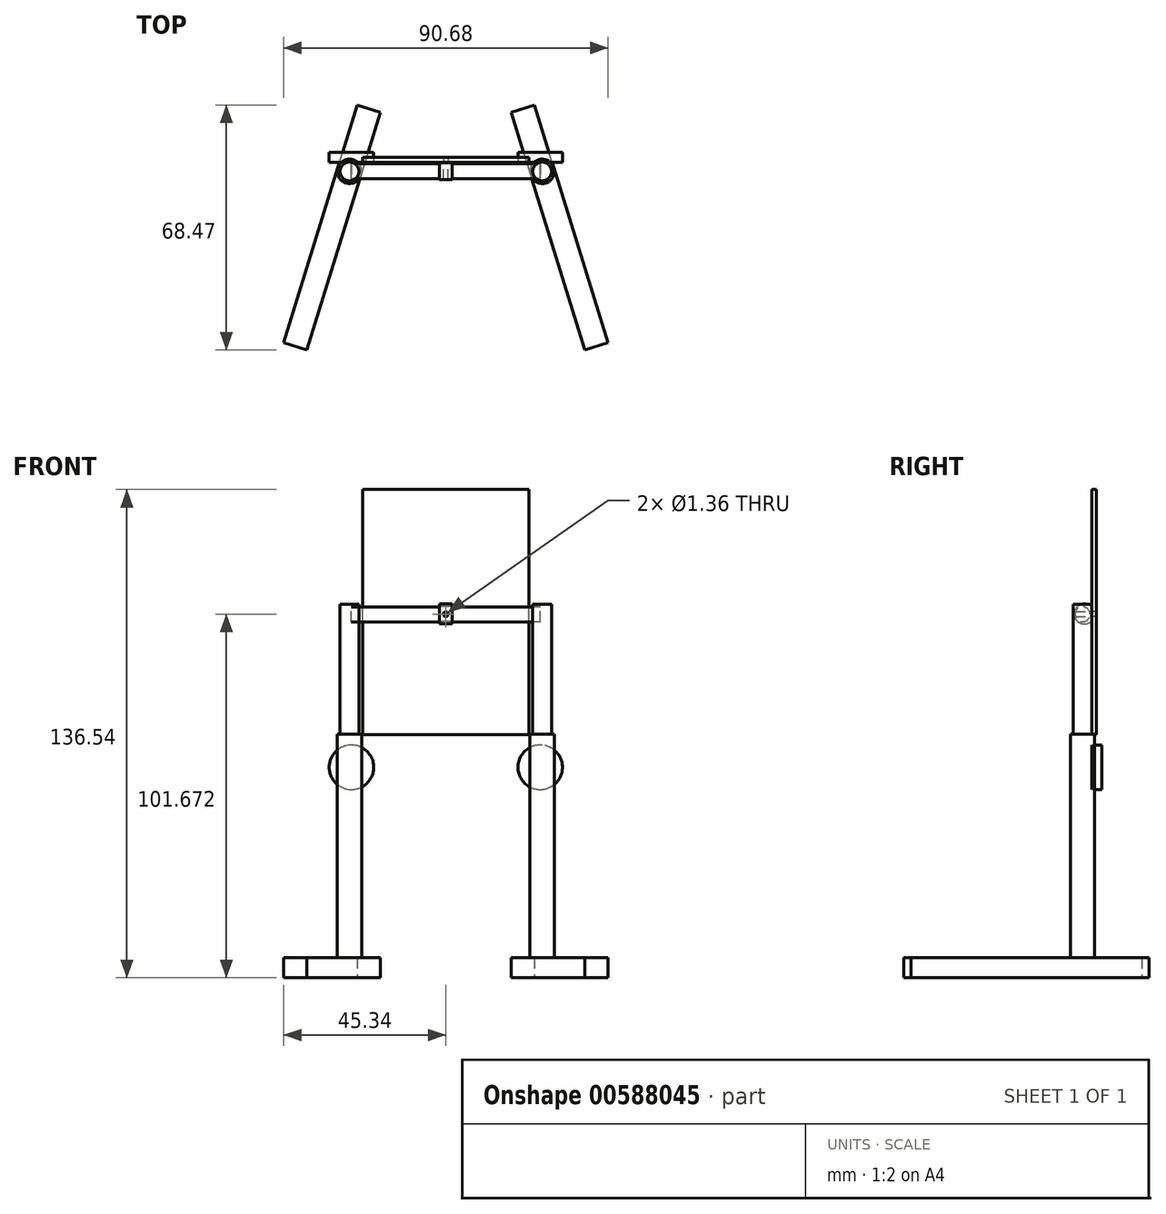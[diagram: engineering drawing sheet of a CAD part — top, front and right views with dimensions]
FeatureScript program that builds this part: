
annotation { "Feature Type Name" : "Feature", "Feature Type Description" : "" }
export const myFeature = defineFeature(function(context is Context, id is Id, definition is map)
    precondition{}
    {
        {
            var Q0;
            Q0=qCreatedBy(makeId("Top.planeOp"),FACE);
            var sketch = newSketch(context, id + "F0", { "sketchPlane" : qUnion([Q0])});
            skLineSegment(sketch, "E0", {"start": v(0, 65.45) * mm, "end": v(0, -72.9) * mm, "construction": true});
            skLineSegment(sketch, "E1", {"start": v(18.26, 16.52) * mm, "end": v(38.84, -49.94) * mm});
            skLineSegment(sketch, "E2", {"start": v(38.84, -49.94) * mm, "end": v(45.34, -47.93) * mm});
            skLineSegment(sketch, "E3", {"start": v(45.34, -47.93) * mm, "end": v(24.75, 18.53) * mm});
            skLineSegment(sketch, "E4", {"start": v(24.75, 18.53) * mm, "end": v(18.26, 16.52) * mm});
            skLineSegment(sketch, "E5.MirrorCS", {"start": v(-45.34, -47.93) * mm, "end": v(-24.75, 18.53) * mm});
            skLineSegment(sketch, "E6.MirrorCS", {"start": v(-18.26, 16.52) * mm, "end": v(-38.84, -49.94) * mm});
            skLineSegment(sketch, "E7.MirrorCS", {"start": v(-24.75, 18.53) * mm, "end": v(-18.26, 16.52) * mm});
            skLineSegment(sketch, "E8.MirrorCS", {"start": v(-38.84, -49.94) * mm, "end": v(-45.34, -47.93) * mm});
            skSolve(sketch);
        }
        {
            var Q0;
            Q0 = qSketchRegion(id + "F0", true);
            extrude(context, id + "F1", {"entities" : qUnion([Q0]), "depth" : 5.6 * mm, "offsetDistance" : 25.4 * mm});
        }
        {
            var Q0;
            Q0=makeQuery(id+"F1.opExtrude","CAP_FACE",FACE,{"disambiguationData":[OSD([sQuery(id+"F0.wireOp",EDGE,"E1"),sQuery(id+"F0.wireOp",EDGE,"E2"),sQuery(id+"F0.wireOp",EDGE,"E3"),sQuery(id+"F0.wireOp",EDGE,"E4")])],"isStart":false});
            var sketch = newSketch(context, id + "F2", { "sketchPlane" : qUnion([Q0])});
            skCircle(sketch, "E9", {"center": v(26.93, 0) * mm, "radius": 3.4 * mm});
            skLineSegment(sketch, "E10", {"start": v(0, -70.33) * mm, "end": v(0, 46.92) * mm, "construction": true});
            skCircle(sketch, "E11.MirrorC", {"center": v(-26.93, 0) * mm, "radius": 3.4 * mm});
            skSolve(sketch);
        }
        {
            var Q0;
            Q0 = qSketchRegion(id + "F2", true);
            extrude(context, id + "F3", {"entities" : qUnion([Q0]), "operationType" : NewBodyOperationType.ADD, "depth" : 62.48 * mm, "offsetDistance" : 25.4 * mm});
        }
        {
            var Q0;
            Q0=makeQuery(id+"F3.opExtrude","CAP_FACE",FACE,{"disambiguationData":[OSD([sQuery(id+"F2.wireOp",EDGE,"E9")])],"isStart":false});
            var sketch = newSketch(context, id + "F4", { "sketchPlane" : qUnion([Q0])});
            skCircle(sketch, "E12", {"center": v(26.93, 0) * mm, "radius": 2.64 * mm});
            skLineSegment(sketch, "E13", {"start": v(0, -17.67) * mm, "end": v(0, 19.87) * mm, "construction": true});
            skCircle(sketch, "E14.MirrorC", {"center": v(-26.93, 0) * mm, "radius": 2.64 * mm});
            skSolve(sketch);
        }
        {
            var Q0;
            Q0 = qSketchRegion(id + "F4", true);
            extrude(context, id + "F5", {"entities" : qUnion([Q0]), "depth" : 36.32 * mm, "offsetDistance" : 25.4 * mm});
        }
        {
            var Q0;
            Q0=qCreatedBy(makeId("Right.planeOp"),FACE);
            var sketch = newSketch(context, id + "F6", { "sketchPlane" : qUnion([Q0])});
            skCircle(sketch, "E15", {"center": v(0, 101.64) * mm, "radius": 2.1 * mm});
            skSolve(sketch);
        }
        {
            var Q0;
            Q0 = qSketchRegion(id + "F6", true);
            extrude(context, id + "F7", {"entities" : qUnion([Q0]), "endBound" : BoundingType.SYMMETRIC, "depth" : 52.93 * mm, "offsetDistance" : 25.4 * mm});
        }
        {
            var Q0;
            Q0=qCreatedBy(makeId("Front.planeOp"),FACE);
            cPlane(context, id + "F8", {"entities" : qUnion([Q0]), "cplaneType" : CPlaneType.OFFSET, "offset" : 2.54 * mm, "oppositeDirection" : true, "width" : 152.4 * mm, "height" : 152.4 * mm});
        }
        {
            var Q0;
            Q0=qCreatedBy(id+"F8.planeOp",FACE);
            var sketch = newSketch(context, id + "F9", { "sketchPlane" : qUnion([Q0])});
            skLineSegment(sketch, "E16.bottom", {"start": v(-23.27, 67.95) * mm, "end": v(23.27, 67.95) * mm});
            skLineSegment(sketch, "E16.top", {"start": v(-23.27, 136.54) * mm, "end": v(23.27, 136.54) * mm});
            skLineSegment(sketch, "E16.left", {"start": v(-23.27, 67.95) * mm, "end": v(-23.27, 136.54) * mm});
            skLineSegment(sketch, "E16.right", {"start": v(23.27, 67.95) * mm, "end": v(23.27, 136.54) * mm});
            skPoint(sketch, "E16.middle", {"position": v(0, 102.25) * mm});
            skSolve(sketch);
        }
        {
            var Q0;
            Q0 = qSketchRegion(id + "F9", true);
            extrude(context, id + "F10", {"entities" : qUnion([Q0]), "oppositeDirection" : true, "depth" : 1.37 * mm, "offsetDistance" : 25.4 * mm});
        }
        {
            var Q0;
            Q0=qCreatedBy(id+"F8.planeOp",FACE);
            var sketch = newSketch(context, id + "F11", { "sketchPlane" : qUnion([Q0])});
            skCircle(sketch, "E17", {"center": v(26.38, 58.87) * mm, "radius": 6.22 * mm});
            skLineSegment(sketch, "E18", {"start": v(0, 76.1) * mm, "end": v(0, 30.94) * mm, "construction": true});
            skCircle(sketch, "E19.MirrorC", {"center": v(-26.38, 58.87) * mm, "radius": 6.22 * mm});
            skSolve(sketch);
        }
        {
            var Q0;
            Q0 = qSketchRegion(id + "F11", true);
            extrude(context, id + "F12", {"entities" : qUnion([Q0]), "oppositeDirection" : true, "depth" : 2.8 * mm, "offsetDistance" : 25.4 * mm});
        }
        {
            var Q0;
            Q0=qCreatedBy(makeId("Right.planeOp"),FACE);
            var sketch = newSketch(context, id + "F13", { "sketchPlane" : qUnion([Q0])});
            skArc(sketch, "E20", {"start": v(2.44, 103.78) * mm, "mid": v(-2.32, 101.8) * mm, "end": v(2.37, 99.64) * mm});
            skLineSegment(sketch, "E21", {"start": v(2.44, 103.78) * mm, "end": v(2.37, 99.64) * mm});
            skSolve(sketch);
        }
        {
            var Q0;
            Q0 = qSketchRegion(id + "F13", true);
            extrude(context, id + "F14", {"entities" : qUnion([Q0]), "operationType" : NewBodyOperationType.ADD, "endBound" : BoundingType.SYMMETRIC, "depth" : 3.56 * mm, "offsetDistance" : 25.4 * mm});
        }
        {
            var Q0;
            Q0=qCreatedBy(makeId("Front.planeOp"),FACE);
            var sketch = newSketch(context, id + "F15", { "sketchPlane" : qUnion([Q0])});
            skCircle(sketch, "E22", {"center": v(0, 101.67) * mm, "radius": 0.68 * mm});
            skSolve(sketch);
        }
        {
            var Q0;
            Q0 = qSketchRegion(id + "F15", true);
            extrude(context, id + "F16", {"entities" : qUnion([Q0]), "operationType" : NewBodyOperationType.REMOVE, "depth" : 3.7 * mm, "offsetDistance" : 25.4 * mm});
        }
        {
            var Q0;
            Q0=makeQuery(id+"F16.boolean.opBoolean","COPY",FACE,{"derivedFrom":makeQuery(id+"F16.opExtrude","CAP_FACE",FACE,{"disambiguationData":[OSD([sQuery(id+"F15.wireOp",EDGE,"E22")])],"isStart":true})});
            extrude(context, id + "F17", {"entities" : qUnion([Q0]), "operationType" : NewBodyOperationType.REMOVE, "oppositeDirection" : true, "depth" : 6.12 * mm, "offsetDistance" : 25.4 * mm});
        }
    });
